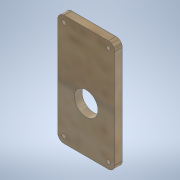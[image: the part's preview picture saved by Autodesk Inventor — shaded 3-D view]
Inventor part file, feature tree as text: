
AUTODESK INVENTOR PART (.ipt)
format: ipt  version: 2020.3 (Build 243373000, 373)  size: 231,936 bytes
history: native  units: mm
features: sketch x4, hole x3, other x1, extrude x1, fillet x1
ambient origin geometry x8: Origin, YZ Plane, XZ Plane, XY Plane, X Axis, Y Axis, Z Axis, Center Point
bodies: Body1 (feature_tree)
feature tree (10):
  other  "ソリッド1"
  extrude  "押し出し1"  Depth=41.0mm
  hole  "穴1"  [1 undecoded]
  fillet  "フィレット1"  Radius=4.5mm
  hole  "穴2"  [1 undecoded]
  hole  "穴3"  [1 undecoded]
  sketch  "スケッチ1"
  sketch  "スケッチ2"
  sketch  "スケッチ3"
  sketch  "スケッチ4"
note: 3 required parameter values undecoded (feature->parameter linkage not recoverable at this tier; creation-order binding heuristic only, values carry confidence <= 0.55)
